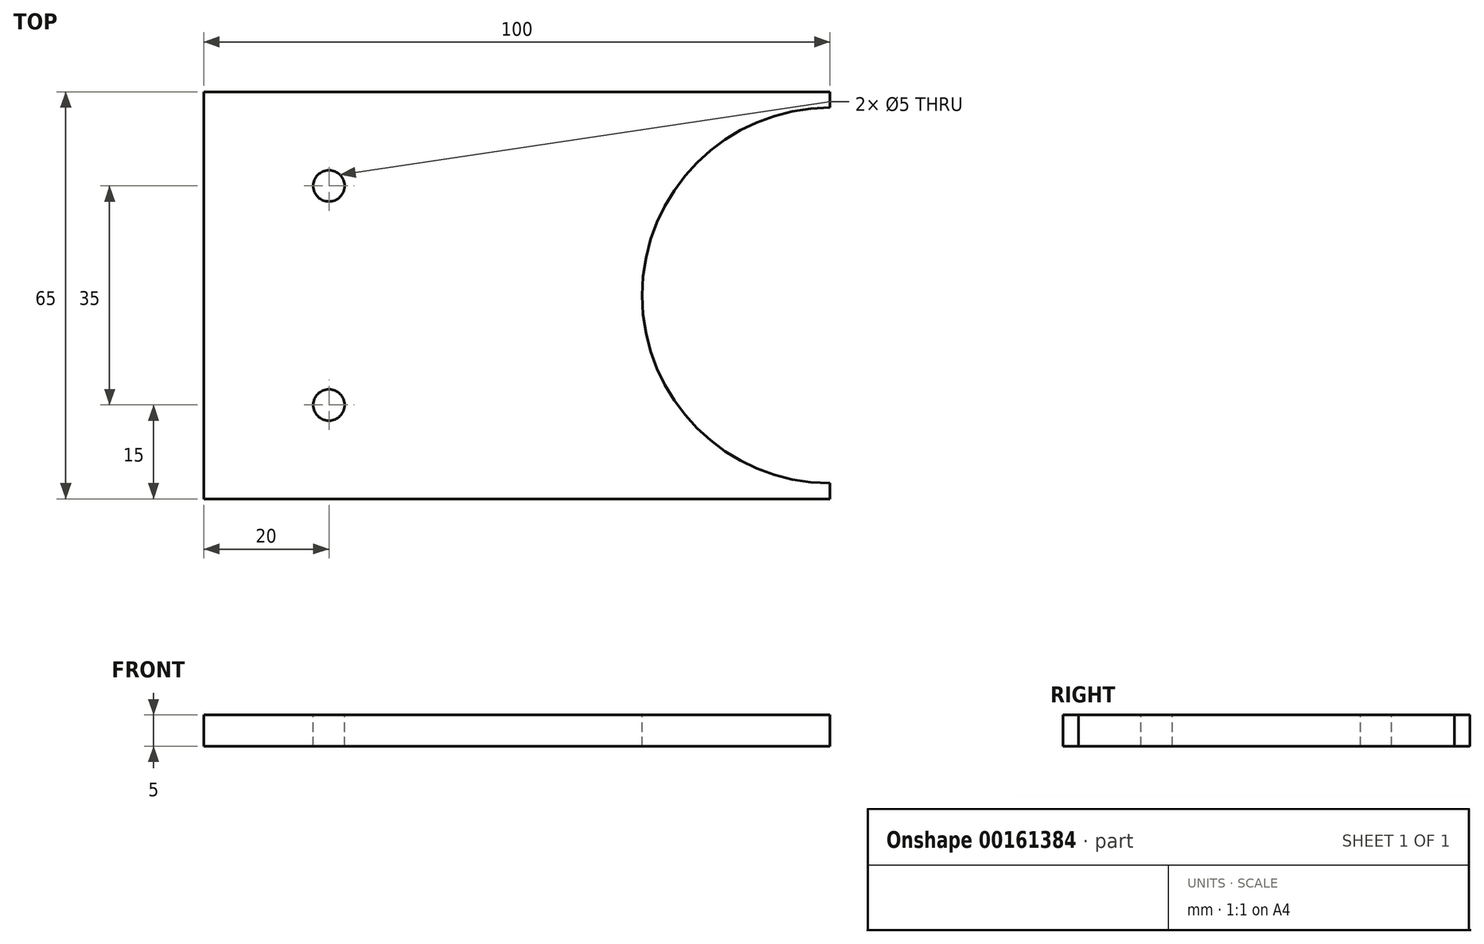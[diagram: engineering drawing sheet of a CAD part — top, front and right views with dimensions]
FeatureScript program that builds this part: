
annotation { "Feature Type Name" : "Feature", "Feature Type Description" : "" }
export const myFeature = defineFeature(function(context is Context, id is Id, definition is map)
    precondition{}
    {
        {
            var Q0;
            Q0=qCreatedBy(makeId("Top.planeOp"),FACE);
            var sketch = newSketch(context, id + "F4", { "sketchPlane" : qUnion([Q0])});
            skLineSegment(sketch, "E0.bottom", {"start": v(50, 32.5) * mm, "end": v(-50, 32.5) * mm});
            skLineSegment(sketch, "E0.top", {"start": v(50, -32.5) * mm, "end": v(-50, -32.5) * mm});
            skLineSegment(sketch, "E0.left", {"start": v(50, 32.5) * mm, "end": v(50, -32.5) * mm});
            skLineSegment(sketch, "E0.right", {"start": v(-50, 32.5) * mm, "end": v(-50, -32.5) * mm});
            skPoint(sketch, "E0.middle", {"position": v(0, 0) * mm});
            skSolve(sketch);
        }
        {
            var Q0;
            Q0 = qSketchRegion(id + "F4", true);
            extrude(context, id + "F0", {"entities" : qUnion([Q0]), "depth" : 5 * mm});
        }
        {
            var Q0;
            Q0=makeQuery(id+"F0.opExtrude","CAP_FACE",FACE,{"disambiguationData":[OSD([sQuery(id+"F4.wireOp",EDGE,"E0.bottom"),sQuery(id+"F4.wireOp",EDGE,"E0.top"),sQuery(id+"F4.wireOp",EDGE,"E0.left"),sQuery(id+"F4.wireOp",EDGE,"E0.right")])],"isStart":false});
            var sketch = newSketch(context, id + "F1", { "sketchPlane" : qUnion([Q0])});
            skCircle(sketch, "E1", {"center": v(50, 0) * mm, "radius": 30 * mm});
            skSolve(sketch);
        }
        {
            var Q0;
            {var subQ0=sQuery(id+"F1.wireOp",EDGE,"E1");var subQ1=makeQuery(id+"F0.opExtrude","CAP_EDGE",EDGE,{"disambiguationData":[OSD([sQuery(id+"F4.wireOp",EDGE,"E0.left")])],"isStart":false});var subQ2=makeQuery(id+"F1.imprint","INTERSECT",VERTEX,{"disambiguationData":[OD(0.0)],"derivedFrom":[subQ1,subQ0]});Q0=makeQuery(id+"F1.imprint","IMPRINT",FACE,{"disambiguationData":[TD([[makeQuery(id+"F1.imprint","IMPRINT",EDGE,{"disambiguationData":[TD([[subQ2,1.0]])],"derivedFrom":subQ0}),1.0]])]});}
            var Q1;
            {var subQ0=sQuery(id+"F1.wireOp",EDGE,"E1");var subQ1=makeQuery(id+"F0.opExtrude","CAP_EDGE",EDGE,{"disambiguationData":[OSD([sQuery(id+"F4.wireOp",EDGE,"E0.left")])],"isStart":false});var subQ2=makeQuery(id+"F1.imprint","INTERSECT",VERTEX,{"disambiguationData":[OD(0.0)],"derivedFrom":[subQ1,subQ0]});Q1=makeQuery(id+"F1.imprint","IMPRINT",FACE,{"disambiguationData":[TD([[makeQuery(id+"F1.imprint","IMPRINT",EDGE,{"disambiguationData":[TD([[subQ2,-1.0]])],"derivedFrom":subQ0}),1.0]])]});}
            extrude(context, id + "F2", {"entities" : qUnion([Q0, Q1]), "operationType" : NewBodyOperationType.REMOVE, "endBound" : BoundingType.THROUGH_ALL, "oppositeDirection" : true, "depth" : 25 * mm});
        }
        {
            var Q0;
            Q0=makeQuery(id+"F0.opExtrude","CAP_FACE",FACE,{"disambiguationData":[OSD([sQuery(id+"F4.wireOp",EDGE,"E0.bottom"),sQuery(id+"F4.wireOp",EDGE,"E0.top"),sQuery(id+"F4.wireOp",EDGE,"E0.left"),sQuery(id+"F4.wireOp",EDGE,"E0.right")])],"isStart":false});
            var sketch = newSketch(context, id + "F3", { "sketchPlane" : qUnion([Q0])});
            skPoint(sketch, "E2", {"position": v(-30, -17.5) * mm});
            skPoint(sketch, "E3", {"position": v(-30, 17.5) * mm});
            skSolve(sketch);
        }
        {
            var Q0;
            Q0=sQuery(id+"F3.wireOp",VERTEX,"E3");
            var Q1;
            Q1=sQuery(id+"F3.wireOp",VERTEX,"E2");
            var Q2;
            Q2=makeQuery(id+"F0.opExtrude","SWEPT_BODY",BODY,{"disambiguationData":[OSD([sQuery(id+"F4.wireOp",EDGE,"E0.bottom"),sQuery(id+"F4.wireOp",EDGE,"E0.top"),sQuery(id+"F4.wireOp",EDGE,"E0.left"),sQuery(id+"F4.wireOp",EDGE,"E0.right")])]});
            hole(context, id + "F5", {"style" : HoleStyle.SIMPLE, "endStyle" : HoleEndStyle.THROUGH, "standardTappedOrClearance" : lookupTablePath({ "standard" : "ISO", "size" : "M6" }), "standardBlindInLast" : lookupTablePath({ "standard" : "ISO", "size" : "M6" }), "holeDiameter" : 5 * mm, "locations" : qUnion([Q0, Q1]), "scope" : qUnion([Q2]), "isTappedThrough" : true});
        }
    });
